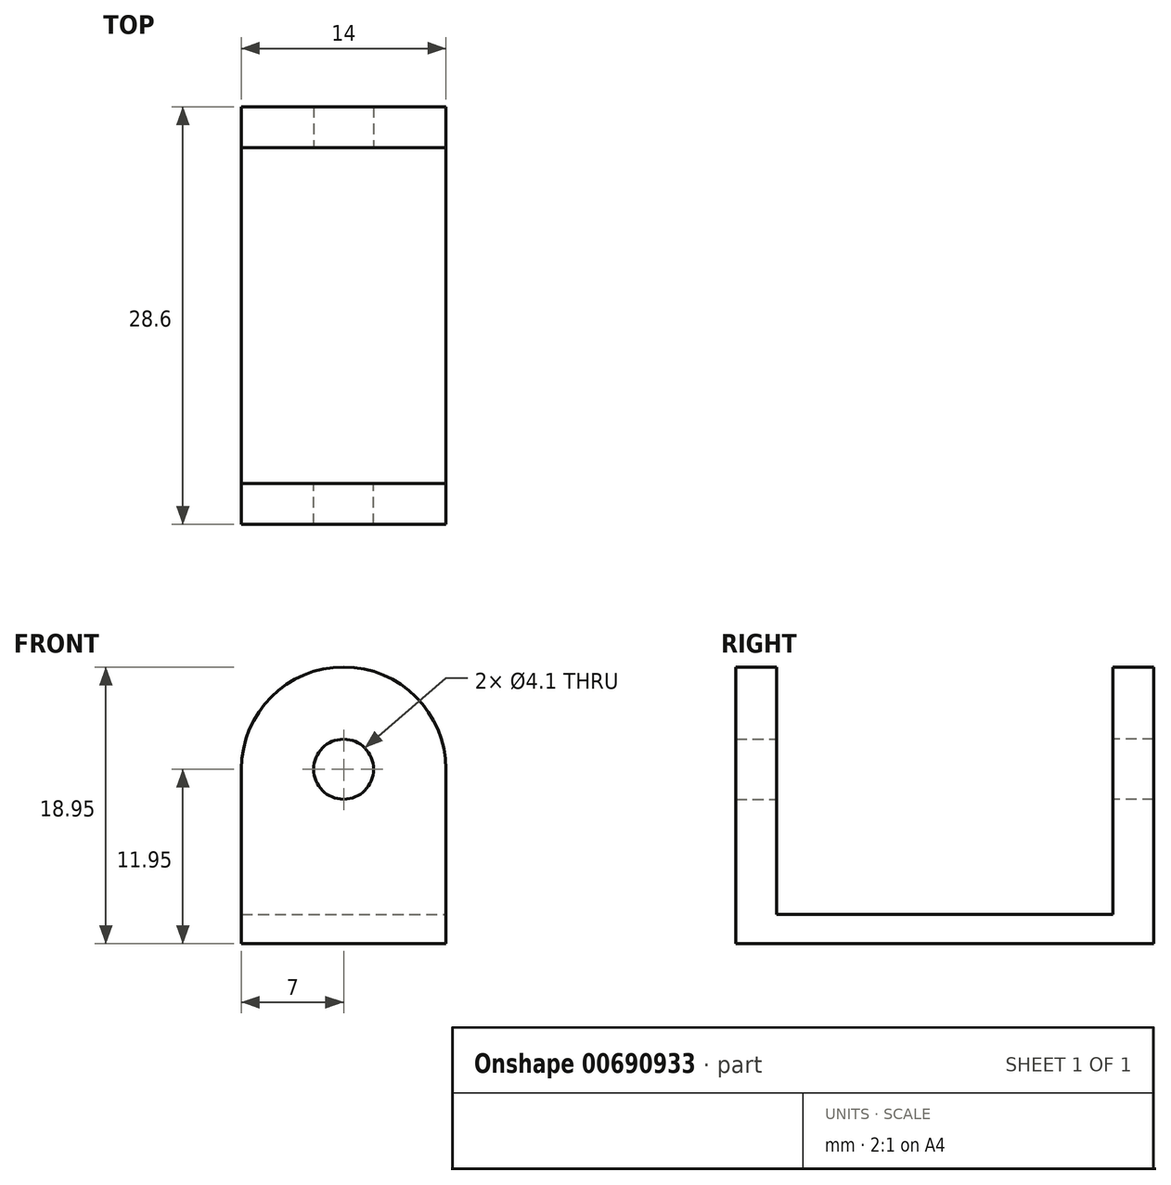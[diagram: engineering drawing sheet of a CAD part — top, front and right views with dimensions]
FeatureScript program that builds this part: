
annotation { "Feature Type Name" : "Feature", "Feature Type Description" : "" }
export const myFeature = defineFeature(function(context is Context, id is Id, definition is map)
    precondition{}
    {
        {
            var Q0;
            Q0=qCreatedBy(makeId("Front.planeOp"),FACE);
            cPlane(context, id + "F0", {"entities" : qUnion([Q0]), "cplaneType" : CPlaneType.OFFSET, "offset" : (22 / 2 + 0.5) * mm, "width" : 150 * mm, "height" : 150 * mm});
        }
        {
            var Q0;
            Q0=qCreatedBy(id+"F0.planeOp",FACE);
            var sketch = newSketch(context, id + "F1", { "sketchPlane" : qUnion([Q0])});
            skLineSegment(sketch, "E0.bottom", {"start": v(-7, 0) * mm, "end": v(7, 0) * mm});
            skLineSegment(sketch, "E0.top", {"start": v(-7, 19) * mm, "end": v(7, 19) * mm, "construction": true});
            skLineSegment(sketch, "E0.left", {"start": v(-7, 0) * mm, "end": v(-7, 11.95) * mm});
            skLineSegment(sketch, "E0.right", {"start": v(7, 0) * mm, "end": v(7, 19) * mm});
            skPoint(sketch, "E0.middle", {"position": v(0, 9.5) * mm});
            skCircle(sketch, "E1", {"center": v(0, 11.95) * mm, "radius": 2.05 * mm});
            skLineSegment(sketch, "E2", {"start": v(7, 11.95) * mm, "end": v(7, 11.95) * mm});
            skArc(sketch, "E3", {"start": v(7, 11.95) * mm, "mid": v(0, 18.95) * mm, "end": v(-7, 11.95) * mm});
            skLineSegment(sketch, "E4", {"start": v(-7, 11.95) * mm, "end": v(-7, 19) * mm});
            skSolve(sketch);
        }
        {
            var Q0;
            Q0 = qSketchRegion(id + "F1", true);
            extrude(context, id + "F2", {"entities" : qUnion([Q0]), "depth" : 2.8 * mm, "offsetDistance" : 25 * mm});
        }
        {
            var Q0;
            Q0=makeQuery(id+"F2.opExtrude","CAP_FACE",FACE,{"disambiguationData":[OSD([sQuery(id+"F1.wireOp",EDGE,"E0.bottom"),sQuery(id+"F1.wireOp",EDGE,"E0.left"),sQuery(id+"F1.wireOp",EDGE,"E0.right"),sQuery(id+"F1.wireOp",EDGE,"E1"),sQuery(id+"F1.wireOp",EDGE,"E3")])],"isStart":true});
            var sketch = newSketch(context, id + "F3", { "sketchPlane" : qUnion([Q0])});
            skLineSegment(sketch, "E5.bottom", {"start": v(7, 0) * mm, "end": v(-7, 0) * mm});
            skLineSegment(sketch, "E5.top", {"start": v(7, 2) * mm, "end": v(-7, 2) * mm});
            skLineSegment(sketch, "E5.left", {"start": v(7, 0) * mm, "end": v(7, 2) * mm});
            skLineSegment(sketch, "E5.right", {"start": v(-7, 0) * mm, "end": v(-7, 2) * mm});
            skSolve(sketch);
        }
        {
            var Q0;
            Q0 = qSketchRegion(id + "F3", true);
            var Q1;
            Q1=qCreatedBy(makeId("Front.planeOp"),FACE);
            extrude(context, id + "F4", {"entities" : qUnion([Q0]), "operationType" : NewBodyOperationType.ADD, "endBound" : BoundingType.UP_TO_SURFACE, "depth" : 25 * mm, "endBoundEntityFace" : qUnion([Q1]), "offsetDistance" : 25 * mm});
        }
        {
            var Q0;
            Q0=makeQuery(id+"F2.opExtrude","SWEPT_BODY",BODY,{"disambiguationData":[OSD([sQuery(id+"F1.wireOp",EDGE,"E0.bottom"),sQuery(id+"F1.wireOp",EDGE,"E0.left"),sQuery(id+"F1.wireOp",EDGE,"E0.right"),sQuery(id+"F1.wireOp",EDGE,"E1"),sQuery(id+"F1.wireOp",EDGE,"E3")])]});
            var Q1;
            Q1=qCreatedBy(makeId("Front.planeOp"),FACE);
            mirror(context, id + "F5", {"operationType" : NewBodyOperationType.ADD, "entities" : qUnion([Q0]), "mirrorPlane" : qUnion([Q1])});
        }
    });
